# Revit family: Genie_Site_VerticalMastLift_GR20a
name_source: partatom
category: Site
revit_build: Autodesk Revit 2018 (Build: 20190510_1515(x64)
units: mm (PartAtom-declared; Revit-internal decimal feet)

## family parameters
Always vertical = Yes
Cut with Voids When Loaded = No
OmniClass Number = 23.50.85.17.11
OmniClass Title = Electric and Battery Telescoping Platforms
Part Type = Normal
Round Connector Dimension = Use Diameter
Shared = No
Work Plane-Based = No

## types (1)
- GR-20
    Assembly Code = E1030900
    AssetType = Fixed
    BIMObjectName = Genie_Site_VerticalMastLift_GR20
    ClassificationName = Uniclass2015
    ClassificationValue = Pr_65_80_47_95
    Color = Grey & Blue
    Cost = 0 $
    Description = The Genie® Runabout® GR™-20 lift is a compact, low-weight machine that increases productivity on the job thanks to its ability to fit through doorways and in most passenger elevators. It can be driven through doorways with operator on board. A zero inside turning radius and full elevation drive features make it ideal for warehousing, transporting, inventory management and general maintenance.
    DocumentationLiterature = https://www.genielift.com
    DocumentationTechnical = https://www.genielift.com
    DurationUnit = Years
    ExpectedLife = 0
    Features = The Genie® Runabout® GR™-20 lift is a compact, low-weight machine that increases productivity on the job thanks to its ability to fit through doorways and in most passenger elevators. It can be driven through doorways with operator on board. A zero inside turning radius and full elevation drive features make it ideal for warehousing, transporting, inventory management and general maintenance.
    Finish = Painted Steel
    IfcExportAs = IfcTransportElement
    IfcExportType = IfcTransportElementType
    Keynote = X
    Manufacturer = Genie
    ManufacturerName = Genie
    Material = Painted Steel
    Model = Genie - Vertical Mast Lifts
    ModelNumber = GR-20
    ModelReference = Genie - Vertical Mast Lifts
    NBSDescription = Vertical lifting platforms
    NBSObjectName = Genie - Vertical lifting platforms
    NBSReference = 90-80-65/350
    NominalDepth = 800 mm
    NominalHeight = 1980 mm
    NominalLength = 1350 mm
    ProductionYear = 2019
    ReplacementCost = 0
    Size = 900mm x 1980mm x 1350mm
    Type Comments = GR-20
    TypeName = Genie - Vertical Mast Lifts
    URL = http://www.genielift.co.uk
    WarrantyDurationLabor = 0
    WarrantyDurationParts = 0
    WarrantyDurationUnit = Years
    WarrantyGuarantorLabor = http://www.genielift.co.uk
    WarrantyGuarantorParts = http://www.genielift.co.uk
    _BSBibleVersion = 15
    _BimSpecGuid = 0
    _CurrentRevision = 0
    _DistributedBy = www.bimstore.co

## geometry (parser evidence)
native form markers: Sweep x9
no freeform markers — native parametric forms only
